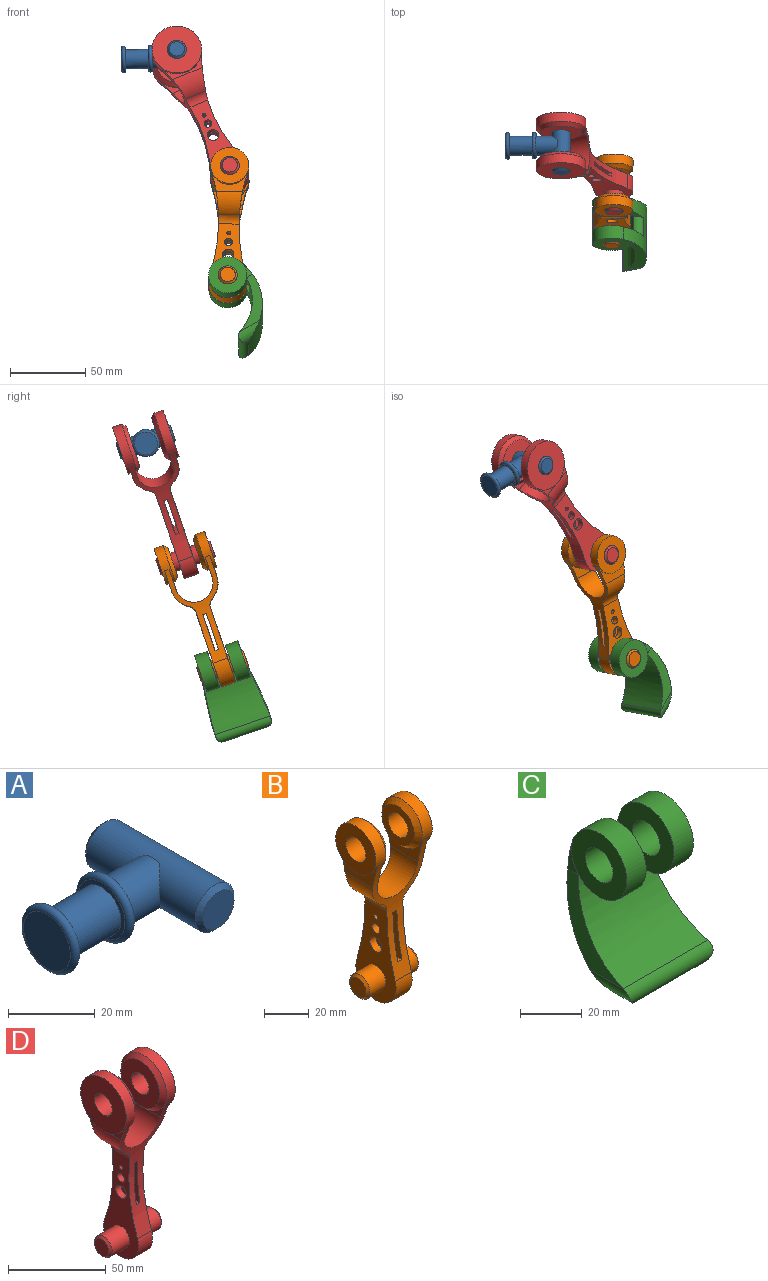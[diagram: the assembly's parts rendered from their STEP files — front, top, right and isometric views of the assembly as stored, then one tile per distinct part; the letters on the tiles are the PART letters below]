
ASSEMBLY  parts=4 mates=3
PART A: 15 faces, bbox 43.2x38.1x19.2 mm
  f0: cylinder r=6.35mm len=15.24mm, axis (-1,0,0), area 608mm2, adj f2,f5
  f1: plane 15.24x15.24mm, normal (-1,0,0), area 182.4mm2, adj f3
  f2: plane 15.24x15.24mm, normal (1,0,0), area 55.7mm2, adj f0,f3
  f3: torus R=7.62mm, axis (-1,0,0), area 211.3mm2, adj f1,f2
  f4: plane 15.24x15.24mm, normal (1,0,0), area 55.7mm2, adj f6,f10
  f5: plane 15.24x15.24mm, normal (-1,0,0), area 55.7mm2, adj f0,f6
  f6: torus R=7.62mm, axis (1,0,0), area 211.3mm2, adj f4,f5
  f7: cylinder r=6.35mm len=35.56mm, axis (0,1,0), area 1269.6mm2, adj f10,f11,f12,f13,f14
  f8: plane 10.16x10.16mm, normal (0,-1,0), area 81.1mm2, adj f14
  f9: plane 10.16x10.16mm, normal (0,1,0), area 81.1mm2, adj f13
  f10: cylinder r=6.35mm len=14.1mm, axis (-1,0,0), area 485.6mm2, adj f4,f7,f11,f12
  f11: plane 4.83x0.48mm, normal (1,0,0), area 1.5mm2, adj f7,f10
  f12: plane 4.83x0.48mm, normal (1,0,0), area 1.5mm2, adj f7,f10
  f13: cone r=6.35mm half-angle=45deg, axis (0,-1,0), area 64.5mm2, adj f7,f9
  f14: cone r=5.08mm half-angle=45deg, axis (0,1,0), area 64.5mm2, adj f7,f8
PART B: 40 faces, bbox 35.6x25.4x101.6 mm
  f0: cylinder r=114.3mm len=68.58mm, axis (-1,0,0), area 576.9mm2, adj f2,f3,f4,f5,f6,f7,f9,f10
  f1: cylinder r=114.3mm len=68.58mm, axis (-1,0,0), area 577mm2, adj f2,f3,f4,f5,f6,f7,f9,f10
  f2: cylinder r=15.88mm len=17.34mm, axis (0,-1,0), area 250.3mm2, adj f0,f1,f3,f9
  f3: cylinder r=6.35mm len=14.09mm, axis (0,-1,0), area 91mm2, adj f0,f1,f2,f10
  f4: cylinder r=6.35mm len=14.09mm, axis (0,-1,0), area 91mm2, adj f0,f1,f5,f11
  f5: cylinder r=15.88mm len=17.34mm, axis (0,-1,0), area 250.3mm2, adj f0,f1,f4,f12
  f6: cylinder r=12.7mm len=25.4mm, axis (0,-1,0), area 604.5mm2, adj f0,f1,f13,f14
  f7: cylinder r=12.7mm len=25.4mm, axis (-1,0,0), area 404.3mm2, adj f0,f1,f12,f13,f17,f22
  f8: cylinder r=6.35mm len=12.7mm, axis (1,0,0), area 354.7mm2, adj f17,f19
  f9: plane 24.23x13.97mm, normal (1,0,0), area 128mm2, adj f0,f1,f2,f15
  f10: plane 52.05x25.4mm, normal (1,0,0), area 757.2mm2, adj f0,f1,f3,f25,f29,f34,f35,f36
  f11: plane 52.05x25.4mm, normal (-1,0,0), area 757.2mm2, adj f0,f1,f4,f24,f29,f37,f38,f39
  f12: plane 24.23x13.97mm, normal (-1,0,0), area 128mm2, adj f0,f1,f5,f7
  f13: plane 24.23x13.97mm, normal (1,0,0), area 128mm2, adj f0,f1,f6,f7
  f14: plane 24.23x13.97mm, normal (-1,0,0), area 128mm2, adj f0,f1,f6,f15
  f15: cylinder r=12.7mm len=25.4mm, axis (-1,0,0), area 404.3mm2, adj f0,f1,f9,f14,f16,f21
  f16: plane 25.4x25.4mm, normal (1,0,0), area 380mm2, adj f15,f18
  f17: plane 25.4x25.4mm, normal (-1,0,0), area 380mm2, adj f7,f8
  f18: cylinder r=6.35mm len=12.7mm, axis (1,0,0), area 354.7mm2, adj f16,f20
  f19: plane 20.32x20.32mm, normal (1,0,0), area 197.6mm2, adj f8,f22
  f20: plane 20.32x20.32mm, normal (-1,0,0), area 197.6mm2, adj f18,f21
  f21: cone r=12.7mm half-angle=45deg, axis (1,0,0), area 258mm2, adj f15,f20
  f22: cone r=10.16mm half-angle=45deg, axis (-1,0,0), area 258mm2, adj f7,f19
  f23: plane 10.16x10.16mm, normal (-1,0,0), area 81.1mm2, adj f28
  f24: cylinder r=6.35mm len=12.7mm, axis (-1,0,0), area 405.4mm2, adj f11,f28
  f25: cylinder r=6.35mm len=12.7mm, axis (-1,0,0), area 405.4mm2, adj f10,f27
  f26: plane 10.16x10.16mm, normal (1,0,0), area 81.1mm2, adj f27
  f27: cone r=5.08mm half-angle=45deg, axis (-1,0,0), area 64.5mm2, adj f25,f26
  f28: cone r=6.35mm half-angle=45deg, axis (1,0,0), area 64.5mm2, adj f23,f24
  f29: cylinder r=12.7mm len=25.4mm, axis (-1,0,0), area 484mm2, adj f0,f1,f10,f11
  f30: plane 20.02x2.54mm, normal (0,0,1), area 50.9mm2, adj f0,f1,f31,f33
  f31: plane 25.4x20.02mm, normal (1,0,0), area 333mm2, adj f0,f1,f30,f32,f37,f38,f39
  f32: plane 13.72x2.54mm, normal (0,0,-1), area 34.8mm2, adj f0,f1,f31,f33
  f33: plane 25.4x20.02mm, normal (-1,0,0), area 333mm2, adj f0,f1,f30,f32,f34,f35,f36
  f34: cylinder r=1.27mm len=3.81mm, axis (1,0,0), area 30.4mm2, adj f10,f33
  f35: cylinder r=2.54mm len=5.08mm, axis (1,0,0), area 60.8mm2, adj f10,f33
  f36: cylinder r=3.81mm len=7.62mm, axis (1,0,0), area 91.2mm2, adj f10,f33
  f37: cylinder r=1.27mm len=3.81mm, axis (1,0,0), area 30.4mm2, adj f11,f31
  f38: cylinder r=2.54mm len=5.08mm, axis (1,0,0), area 60.8mm2, adj f11,f31
  f39: cylinder r=3.81mm len=7.62mm, axis (1,0,0), area 91.2mm2, adj f11,f31
PART C: 19 faces, bbox 39.3x32.7x59.8 mm
  f0: cylinder r=35.56mm len=38.7mm, axis (-1,0,0), area 1425.8mm2, adj f2,f3,f5,f9,f10,f11,f12,f16
  f1: cylinder r=39.21mm len=51.08mm, axis (-1,0,0), area 1807.4mm2, adj f3,f5,f9,f10,f11,f12,f13,f14
  f2: cylinder r=3.81mm len=38.83mm, axis (-1,0,0), area 347.3mm2, adj f0,f12,f13,f14,f15,f16
  f3: cylinder r=12.7mm len=25.4mm, axis (-1,0,0), area 587.1mm2, adj f0,f1,f8,f10
  f4: cylinder r=6.35mm len=12.7mm, axis (-1,0,0), area 354.7mm2, adj f8,f10
  f5: cylinder r=12.7mm len=25.4mm, axis (-1,0,0), area 587mm2, adj f0,f1,f7,f9
  f6: cylinder r=6.35mm len=12.7mm, axis (-1,0,0), area 354.7mm2, adj f7,f9
  f7: plane 25.53x25.52mm, normal (1,0,0), area 380mm2, adj f5,f6,f16,f18
  f8: plane 25.53x25.51mm, normal (-1,0,0), area 380mm2, adj f3,f4,f17
  f9: plane 31.7x27.07mm, normal (-1,0,0), area 430.2mm2, adj f0,f1,f5,f6,f11
  f10: plane 31.7x27.07mm, normal (1,0,0), area 430.2mm2, adj f0,f1,f3,f4,f11
  f11: cylinder r=5.08mm len=12.7mm, axis (1,0,0), area 109.3mm2, adj f0,f1,f9,f10
  f12: plane 31.19x30.26mm, normal (-0.99,0,0.13), area 244.2mm2, adj f0,f1,f2,f13,f17
  f13: cylinder r=6.35mm len=18.11mm, axis (0,1,0), area 113.9mm2, adj f1,f2,f12,f14
  f14: plane 26.13x2.31mm, normal (0,0,-1), area 60.4mm2, adj f1,f2,f13,f15
  f15: cylinder r=6.35mm len=18.11mm, axis (0,1,0), area 113.8mm2, adj f1,f2,f14,f16
  f16: plane 31.51x30.28mm, normal (0.99,0,0.13), area 245.9mm2, adj f0,f1,f2,f7,f15,f18
  f17: plane 13.14x4.9mm, normal (-1,0,0), area 21.3mm2, adj f0,f1,f8,f12
  f18: plane 12.87x4.87mm, normal (1,0,0), area 19.8mm2, adj f1,f7,f16
PART D: 40 faces, bbox 38.1x33x118.1 mm
  f0: cylinder r=101.6mm len=77.6mm, axis (-1,0,0), area 688.9mm2, adj f2,f3,f4,f5,f6,f7,f9,f10
  f1: cylinder r=101.6mm len=77.61mm, axis (-1,0,0), area 689.2mm2, adj f2,f3,f4,f5,f6,f7,f9,f10
  f2: cylinder r=15.88mm len=21.45mm, axis (0,-1,0), area 283.9mm2, adj f0,f1,f3,f9
  f3: cylinder r=6.35mm len=14.56mm, axis (0,-1,0), area 89.9mm2, adj f0,f1,f2,f10
  f4: cylinder r=6.35mm len=14.56mm, axis (0,-1,0), area 89.9mm2, adj f0,f1,f5,f11
  f5: cylinder r=15.88mm len=21.45mm, axis (0,-1,0), area 283.9mm2, adj f0,f1,f4,f12
  f6: cylinder r=12.7mm len=25.4mm, axis (0,-1,0), area 680mm2, adj f0,f1,f13,f14
  f7: cylinder r=16.51mm len=33.02mm, axis (-1,0,0), area 539mm2, adj f0,f1,f12,f13,f17,f22
  f8: cylinder r=6.35mm len=12.7mm, axis (1,0,0), area 354.7mm2, adj f17,f19
  f9: plane 29.99x10.87mm, normal (1,0,0), area 70.1mm2, adj f0,f1,f2,f15
  f10: plane 64.75x25.4mm, normal (1,0,0), area 856.2mm2, adj f0,f1,f3,f25,f29,f34,f35,f36
  f11: plane 64.75x25.4mm, normal (-1,0,0), area 856.2mm2, adj f0,f1,f4,f24,f29,f37,f38,f39
  f12: plane 29.99x10.87mm, normal (-1,0,0), area 70.1mm2, adj f0,f1,f5,f7
  f13: plane 29.99x10.87mm, normal (1,0,0), area 70.1mm2, adj f0,f1,f6,f7
  f14: plane 29.99x10.87mm, normal (-1,0,0), area 70.1mm2, adj f0,f1,f6,f15
  f15: cylinder r=16.51mm len=33.02mm, axis (-1,0,0), area 539mm2, adj f0,f1,f9,f14,f16,f21
  f16: plane 33.02x33.02mm, normal (1,0,0), area 729.7mm2, adj f15,f18
  f17: plane 33.02x33.02mm, normal (-1,0,0), area 729.7mm2, adj f7,f8
  f18: cylinder r=6.35mm len=12.7mm, axis (1,0,0), area 354.7mm2, adj f16,f20
  f19: plane 27.94x27.94mm, normal (1,0,0), area 486.4mm2, adj f8,f22
  f20: plane 27.94x27.94mm, normal (-1,0,0), area 486.4mm2, adj f18,f21
  f21: cone r=16.51mm half-angle=45deg, axis (1,0,0), area 344mm2, adj f15,f20
  f22: cone r=13.97mm half-angle=45deg, axis (-1,0,0), area 344mm2, adj f7,f19
  f23: plane 10.16x10.16mm, normal (-1,0,0), area 81.1mm2, adj f28
  f24: cylinder r=6.35mm len=12.7mm, axis (-1,0,0), area 506.7mm2, adj f11,f28
  f25: cylinder r=6.35mm len=12.7mm, axis (-1,0,0), area 506.7mm2, adj f10,f27
  f26: plane 10.16x10.16mm, normal (1,0,0), area 81.1mm2, adj f27
  f27: cone r=5.08mm half-angle=45deg, axis (-1,0,0), area 64.5mm2, adj f25,f26
  f28: cone r=6.35mm half-angle=45deg, axis (1,0,0), area 64.5mm2, adj f23,f24
  f29: cylinder r=12.7mm len=25.4mm, axis (-1,0,0), area 496.4mm2, adj f0,f1,f10,f11
  f30: plane 14.52x2.54mm, normal (0,0,1), area 36.9mm2, adj f0,f1,f31,f33
  f31: plane 25.4x14.52mm, normal (1,0,0), area 237.3mm2, adj f0,f1,f30,f32,f37,f38,f39
  f32: plane 11.89x2.54mm, normal (0,0,-1), area 30.2mm2, adj f0,f1,f31,f33
  f33: plane 25.4x14.52mm, normal (-1,0,0), area 237.3mm2, adj f0,f1,f30,f32,f34,f35,f36
  f34: cylinder r=1.27mm len=3.81mm, axis (1,0,0), area 30.4mm2, adj f10,f33
  f35: cylinder r=2.54mm len=5.08mm, axis (1,0,0), area 60.8mm2, adj f10,f33
  f36: cylinder r=3.81mm len=7.62mm, axis (1,0,0), area 91.2mm2, adj f10,f33
  f37: cylinder r=1.27mm len=3.81mm, axis (1,0,0), area 30.4mm2, adj f11,f31
  f38: cylinder r=2.54mm len=5.08mm, axis (1,0,0), area 60.8mm2, adj f11,f31
  f39: cylinder r=3.81mm len=7.62mm, axis (1,0,0), area 91.2mm2, adj f11,f31
PLACE A rot(axis=(-1,-0.08,0),18.9deg) t=(250.62,24.53,65.37)mm fixed
PLACE B rot(axis=(-0.17,-0.15,-0.97),91.9deg) t=(304.9,-1.86,-11.36)mm
PLACE C rot(axis=(0.11,-0.43,-0.9),91deg) t=(303.55,-26.43,-83.47)mm
PLACE D rot(axis=(0.04,-0.36,-0.93),90.3deg) t=(269.66,24.61,65.84)mm
MATE revolute C.f3 <-> B.f24  axis (0,0.95,-0.32) through (303.52,-32.44,-81.43)mm
MATE revolute A.f7 <-> D.f7  axis (0,-0.95,0.32) through (269.59,7.78,71.58)mm
MATE revolute D.f24 <-> B.f7  axis (0,-0.95,0.32) through (304.83,-18.69,-5.62)mm
